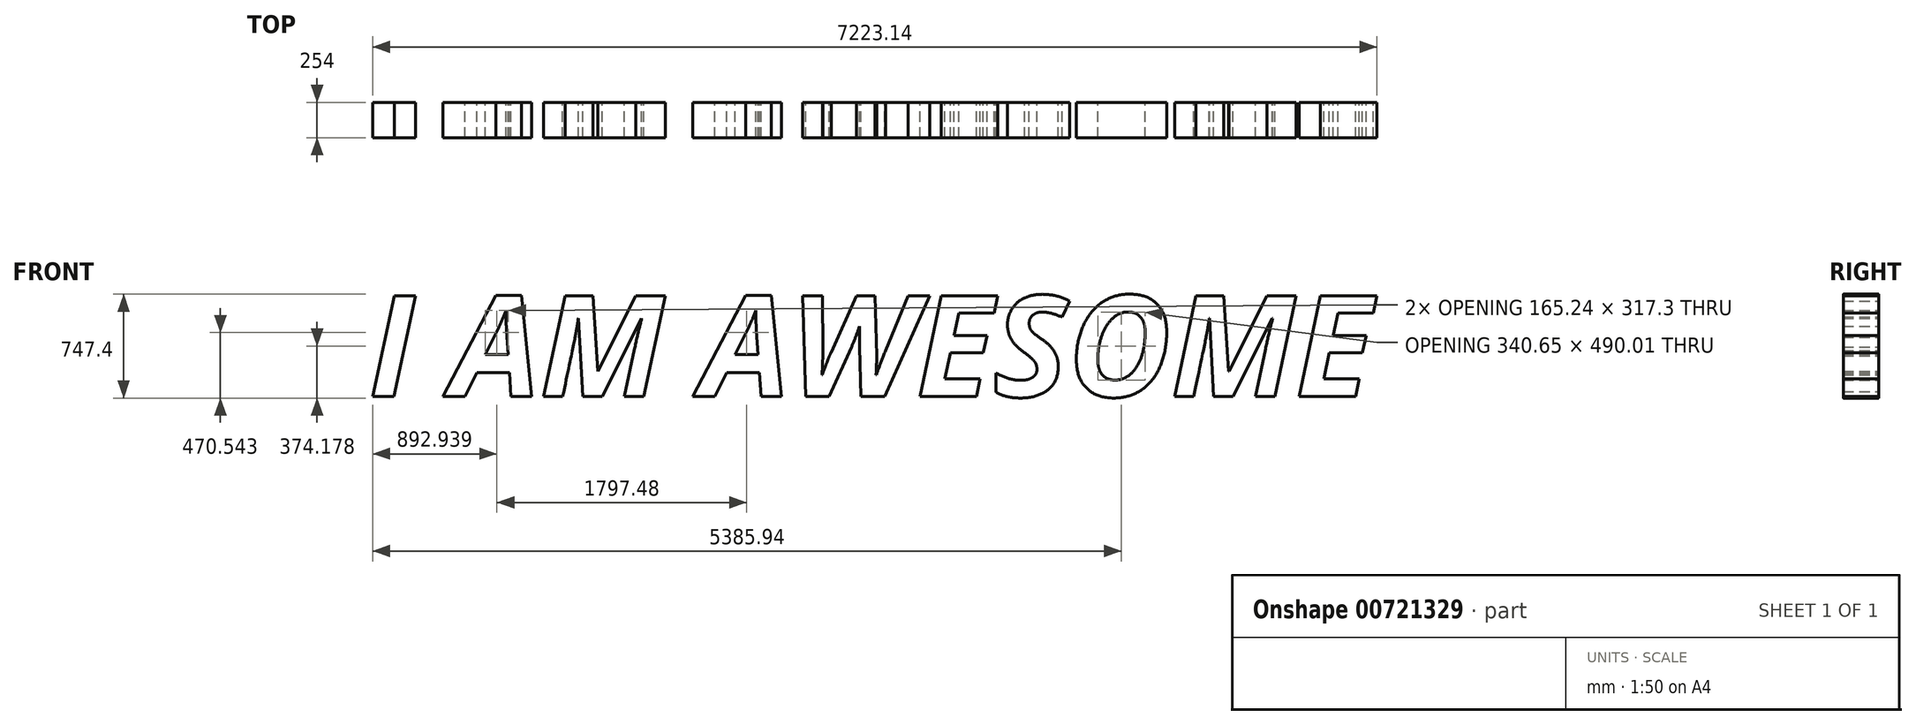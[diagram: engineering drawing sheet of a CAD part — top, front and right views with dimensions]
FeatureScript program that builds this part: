
annotation { "Feature Type Name" : "Feature", "Feature Type Description" : "" }
export const myFeature = defineFeature(function(context is Context, id is Id, definition is map)
    precondition{}
    {
        {
            var Q0;
            Q0=qCreatedBy(makeId("Front.planeOp"),FACE);
            var sketch = newSketch(context, id + "F0", { "sketchPlane" : qUnion([Q0])});
            skText(sketch, "E0", { "text": "I AM AWESOME", "fontName": "OpenSans-BoldItalic.ttf"});
            const initialGuessF0  = {"E0": [-0.07111, -0.64552, 1, 0, 0.73215]};
            skSetInitialGuess(sketch, initialGuessF0);
            skSolve(sketch);
        }
        {
            var Q0;
            Q0 = qSketchRegion(id + "F0", true);
            extrude(context, id + "F1", {"entities" : qUnion([Q0]), "depth" : 254 * mm, "offsetDistance" : 25.4 * mm});
        }
    });
